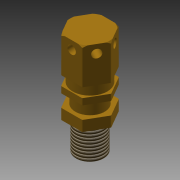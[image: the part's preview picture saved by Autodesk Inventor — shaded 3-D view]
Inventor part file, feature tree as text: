
AUTODESK INVENTOR PART (.ipt)
format: ipt  version: 2016 SP1 (Build 200210100, 210)  size: 202,752 bytes
history: native  units: mm (DEFAULTED — no unit token found)
features: sketch x9, projected_geometry x9, extrude x8, pattern_circular x1, thread x1, fillet x1, revolve x1
ambient origin geometry x8: Origin, YZ Plane, XZ Plane, XY Plane, X Axis, Y Axis, Z Axis, Center Point
bodies: Solid1 (feature_tree)
feature tree (30):
  extrude  "Extrusion1"  Depth=17.0mm TaperAngle=0.0deg
  extrude  "Extrusion2"  Depth=4.5mm TaperAngle=0.0deg
  extrude  "Extrusion3"  Depth=14.0mm
  extrude  "Extrusion4"  Depth=5.0mm TaperAngle=0.0deg
  extrude  "Extrusion5"  Depth=14.5mm TaperAngle=0.0deg
  extrude  "Extrusion6"  Depth=47.5mm TaperAngle=0.0deg
  extrude  "Extrusion7"  Depth=4.0mm
  extrude  "Extrusion8"  Depth=30.0mm TaperAngle=360.0deg
  pattern_circular  "Circular Pattern1"  Angle=45.0deg  [1 undecoded]
  thread  "Thread1"  [1 undecoded]
  fillet  "Fillet1"  [1 undecoded]
  revolve  "Revolution2"  [1 undecoded]
  sketch  "Sketch1"  dims[d0=17.5mm d1=17.0mm d2=0.0mm]
  sketch  "Sketch2"  dims[d3=16.5mm d4=4.5mm d5=0.0mm]
  projected_geometry  "Projected Loop1"
  sketch  "Sketch3"  dims[d6=3.0mm d7=0.0mm d8=14.0mm]
  projected_geometry  "Projected Loop2"
  sketch  "Sketch4"  dims[d9=6.0mm d10=0.0mm d11=5.0mm d12=0.0mm]
  projected_geometry  "Projected Loop3"
  sketch  "Sketch5"  dims[d13=13.25mm d14=14.5mm d15=0.0mm]
  projected_geometry  "Projected Loop4"
  sketch  "Sketch6"  dims[d16=5.0mm d17=47.5mm d18=0.0mm]
  projected_geometry  "Projected Loop5"
  sketch  "Sketch7"  dims[d19=4.0mm d20=4.0mm]
  projected_geometry  "Projected Loop6"
  sketch  "Sketch8"  dims[d21=40.25mm d22=0.0mm d23=30.0mm d25=360.0deg]
  projected_geometry  "Projected Loop7"
  sketch  "Sketch10"  dims[d26=10.0mm d27=0.0mm d28=0.5mm d32=45.0deg d33=1.0mm d34=90.0deg]
  projected_geometry  "Projected Loop8"
  projected_geometry  "Projected Loop9"
note: 4 required parameter values undecoded (feature->parameter linkage not recoverable at this tier; creation-order binding heuristic only, values carry confidence <= 0.55)
